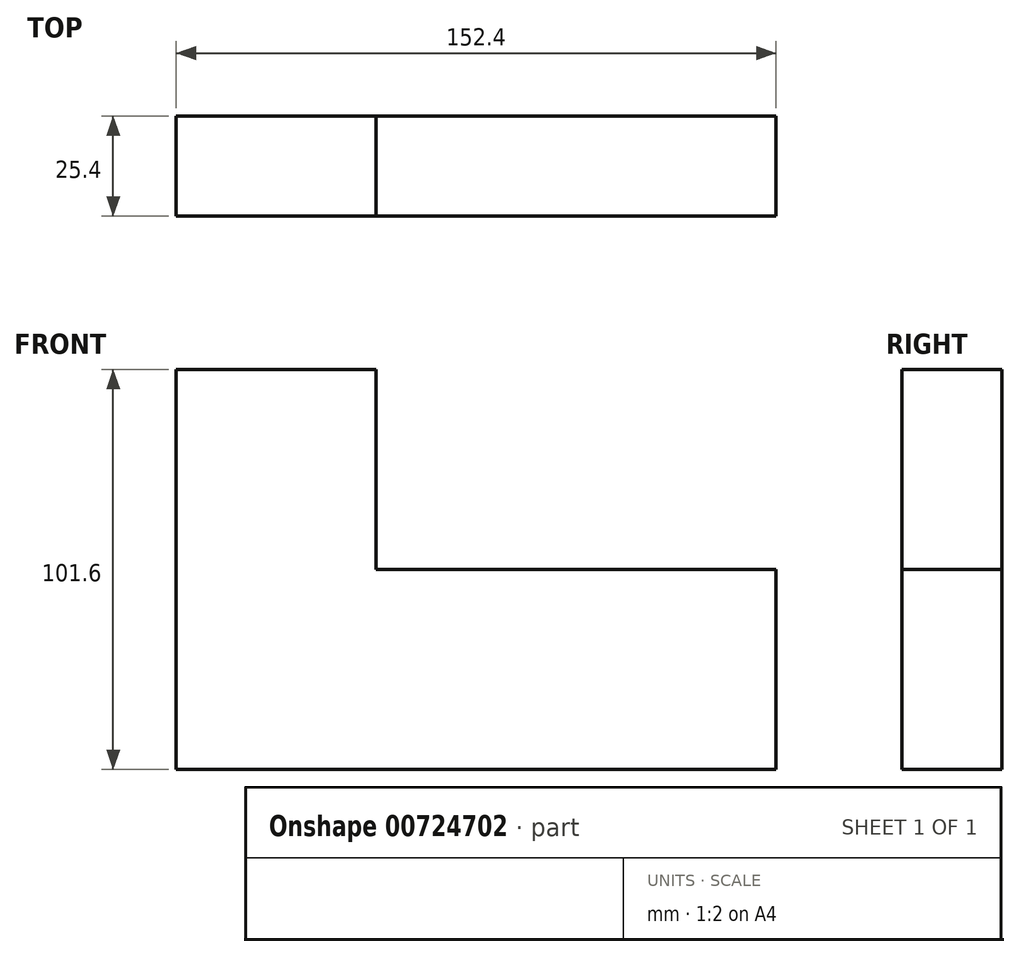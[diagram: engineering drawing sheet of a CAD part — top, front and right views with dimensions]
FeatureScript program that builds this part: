
annotation { "Feature Type Name" : "Feature", "Feature Type Description" : "" }
export const myFeature = defineFeature(function(context is Context, id is Id, definition is map)
    precondition{}
    {
        {
            var Q0;
            Q0=qCreatedBy(makeId("Front.planeOp"),FACE);
            var sketch = newSketch(context, id + "F0", { "sketchPlane" : qUnion([Q0])});
            skLineSegment(sketch, "E0", {"start": v(-92.71, -28.76) * mm, "end": v(59.69, -28.76) * mm});
            skLineSegment(sketch, "E1", {"start": v(59.69, -28.76) * mm, "end": v(59.69, 22.04) * mm});
            skLineSegment(sketch, "E2", {"start": v(59.69, 22.04) * mm, "end": v(-41.91, 22.04) * mm});
            skLineSegment(sketch, "E3", {"start": v(-41.91, 22.04) * mm, "end": v(-41.91, 72.84) * mm});
            skLineSegment(sketch, "E4", {"start": v(-41.91, 72.84) * mm, "end": v(-92.71, 72.84) * mm});
            skLineSegment(sketch, "E5", {"start": v(-92.71, 72.84) * mm, "end": v(-92.71, -28.76) * mm});
            skSolve(sketch);
        }
        {
            var Q0;
            Q0 = qSketchRegion(id + "F0", true);
            extrude(context, id + "F1", {"entities" : qUnion([Q0]), "depth" : 25.4 * mm, "offsetDistance" : 25.4 * mm});
        }
    });
